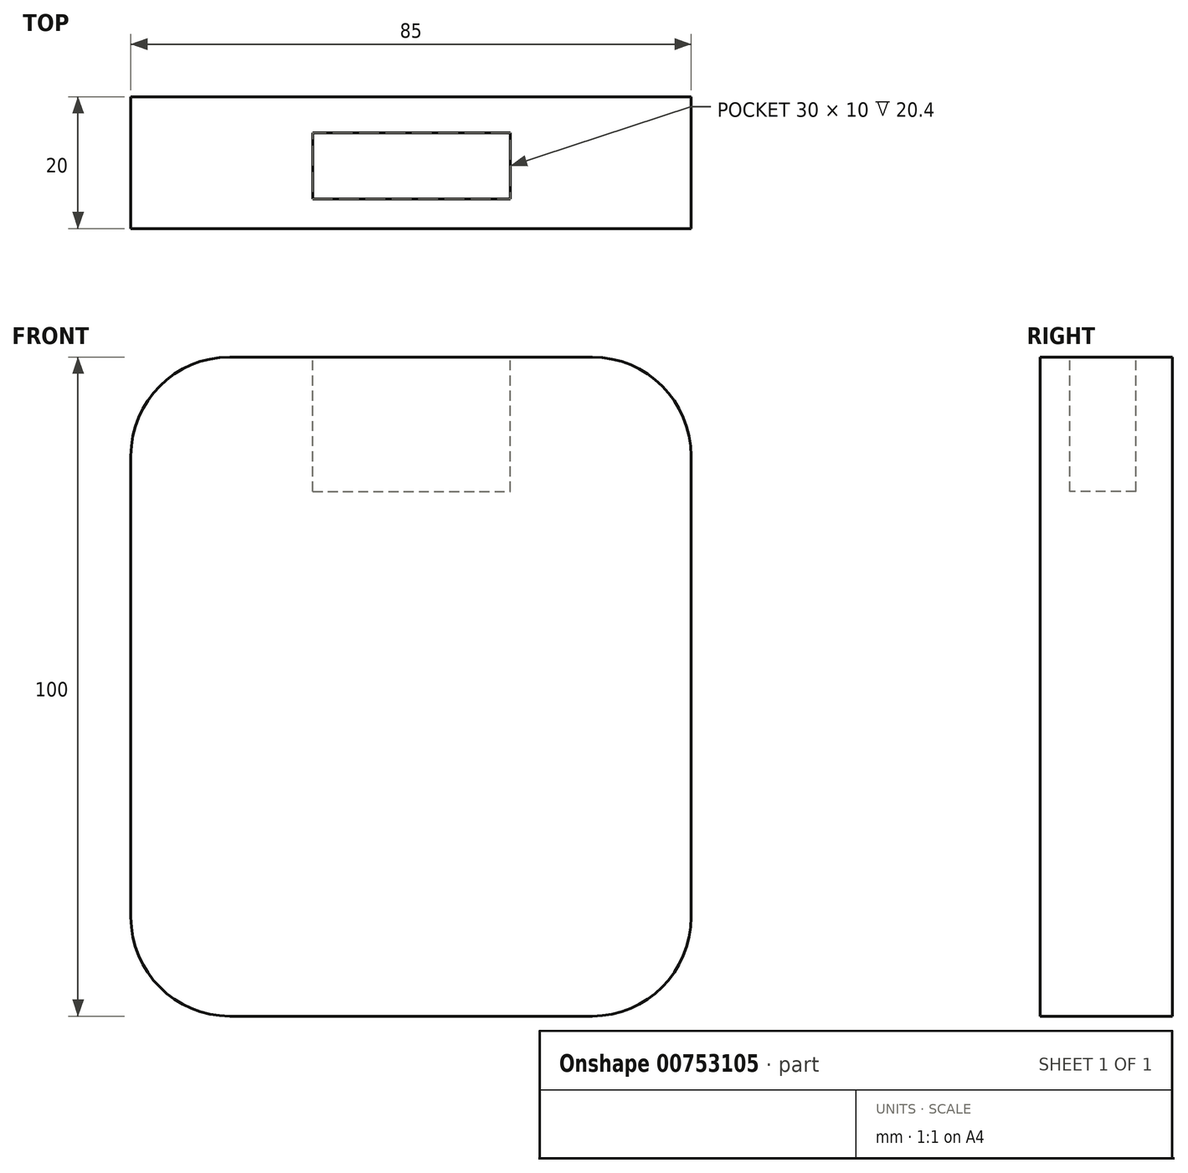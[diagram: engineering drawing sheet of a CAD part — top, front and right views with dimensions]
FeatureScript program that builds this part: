
annotation { "Feature Type Name" : "Feature", "Feature Type Description" : "" }
export const myFeature = defineFeature(function(context is Context, id is Id, definition is map)
    precondition{}
    {
        {
            var Q0;
            Q0=qCreatedBy(makeId("Front.planeOp"),FACE);
            var sketch = newSketch(context, id + "F0", { "sketchPlane" : qUnion([Q0])});
            skLineSegment(sketch, "E0.bottom", {"start": v(-38.39, 35.38) * mm, "end": v(46.61, 35.38) * mm});
            skLineSegment(sketch, "E0.top", {"start": v(-38.39, -64.62) * mm, "end": v(46.61, -64.62) * mm});
            skLineSegment(sketch, "E0.left", {"start": v(-38.39, 35.38) * mm, "end": v(-38.39, -64.62) * mm});
            skLineSegment(sketch, "E0.right", {"start": v(46.61, 35.38) * mm, "end": v(46.61, -64.62) * mm});
            skSolve(sketch);
        }
        {
            var Q0;
            Q0=makeQuery(id+"F0.imprint","IMPRINT",FACE,{"disambiguationData":[TD([[makeQuery(id+"F0.imprint","IMPRINT",EDGE,{"derivedFrom":sQuery(id+"F0.wireOp",EDGE,"E0.bottom")}),-1.0]])]});
            extrude(context, id + "F1", {"entities" : qUnion([Q0]), "depth" : 20 * mm, "offsetDistance" : 25 * mm});
        }
        {
            var Q0;
            Q0=makeQuery(id+"F1.opExtrude","SWEPT_FACE",FACE,{"disambiguationData":[OSD([sQuery(id+"F0.wireOp",EDGE,"E0.bottom")])]});
            var sketch = newSketch(context, id + "F2", { "sketchPlane" : qUnion([Q0])});
            skLineSegment(sketch, "E1.bottom", {"start": v(-10.79, -5.5) * mm, "end": v(19.21, -5.5) * mm});
            skLineSegment(sketch, "E1.top", {"start": v(-10.79, -15.5) * mm, "end": v(19.21, -15.5) * mm});
            skLineSegment(sketch, "E1.left", {"start": v(-10.79, -5.5) * mm, "end": v(-10.79, -15.5) * mm});
            skLineSegment(sketch, "E1.right", {"start": v(19.21, -5.5) * mm, "end": v(19.21, -15.5) * mm});
            skSolve(sketch);
        }
        {
            var Q0;
            Q0 = qSketchRegion(id + "F2", true);
            extrude(context, id + "F3", {"entities" : qUnion([Q0]), "operationType" : NewBodyOperationType.REMOVE, "oppositeDirection" : true, "depth" : 20.4 * mm, "offsetDistance" : 25 * mm});
        }
        {
            var Q0;
            Q0=makeQuery(id+"F1.opExtrude","SWEPT_EDGE",EDGE,{"disambiguationData":[OSD([sQuery(id+"F0.wireOp",EDGE,"E0.bottom"),sQuery(id+"F0.wireOp",EDGE,"E0.right")])]});
            var Q1;
            Q1=makeQuery(id+"F1.opExtrude","SWEPT_EDGE",EDGE,{"disambiguationData":[OSD([sQuery(id+"F0.wireOp",EDGE,"E0.bottom"),sQuery(id+"F0.wireOp",EDGE,"E0.left")])]});
            var Q2;
            Q2=makeQuery(id+"F1.opExtrude","SWEPT_EDGE",EDGE,{"disambiguationData":[OSD([sQuery(id+"F0.wireOp",EDGE,"E0.top"),sQuery(id+"F0.wireOp",EDGE,"E0.right")])]});
            var Q3;
            Q3=makeQuery(id+"F1.opExtrude","SWEPT_EDGE",EDGE,{"disambiguationData":[OSD([sQuery(id+"F0.wireOp",EDGE,"E0.top"),sQuery(id+"F0.wireOp",EDGE,"E0.left")])]});
            fillet(context, id + "F4", {"entities" : qUnion([Q0, Q1, Q2, Q3]), "radius" : 15 * mm, "tangentPropagation" : true, "allowEdgeOverflow" : false});
        }
    });
